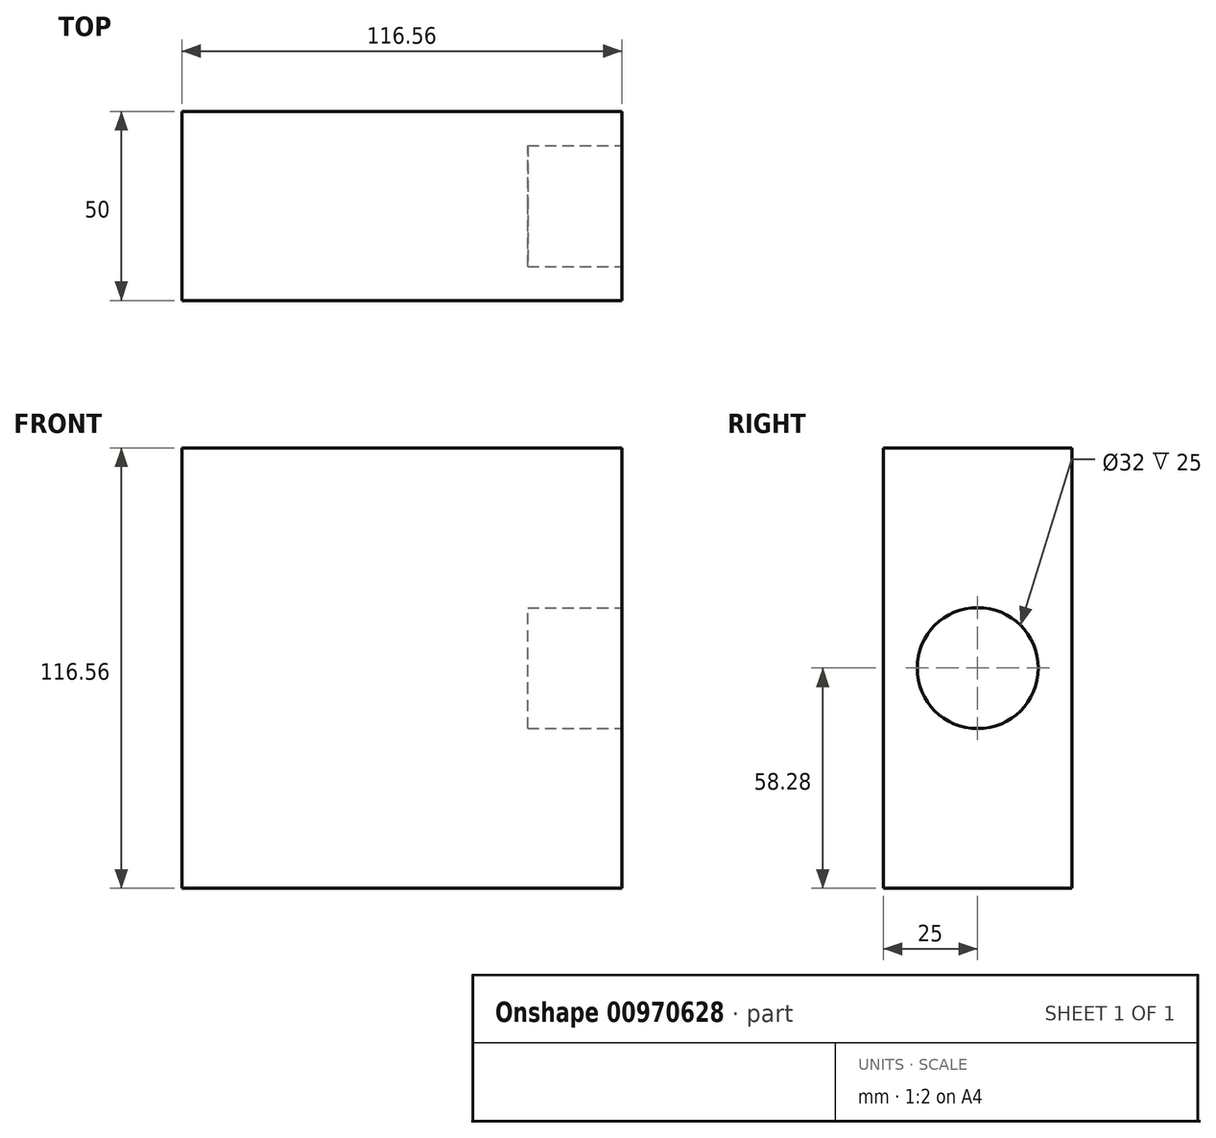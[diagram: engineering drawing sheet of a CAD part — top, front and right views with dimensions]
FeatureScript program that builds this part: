
annotation { "Feature Type Name" : "Feature", "Feature Type Description" : "" }
export const myFeature = defineFeature(function(context is Context, id is Id, definition is map)
    precondition{}
    {
        {
            var Q0;
            Q0=qCreatedBy(makeId("Front.planeOp"),FACE);
            var sketch = newSketch(context, id + "F0", { "sketchPlane" : qUnion([Q0])});
            skLineSegment(sketch, "E0.bottom", {"start": v(58.28, -58.28) * mm, "end": v(-58.28, -58.28) * mm});
            skLineSegment(sketch, "E0.top", {"start": v(58.28, 58.28) * mm, "end": v(-58.28, 58.28) * mm});
            skLineSegment(sketch, "E0.left", {"start": v(58.28, -58.28) * mm, "end": v(58.28, 58.28) * mm});
            skLineSegment(sketch, "E0.right", {"start": v(-58.28, -58.28) * mm, "end": v(-58.28, 58.28) * mm});
            skPoint(sketch, "E0.middle", {"position": v(0, 0) * mm});
            skSolve(sketch);
        }
        {
            var Q0;
            Q0=makeQuery(id+"F0.imprint","IMPRINT",FACE,{"disambiguationData":[TD([[makeQuery(id+"F0.imprint","IMPRINT",EDGE,{"derivedFrom":sQuery(id+"F0.wireOp",EDGE,"E0.bottom")}),-1.0]])]});
            extrude(context, id + "F1", {"entities" : qUnion([Q0]), "depth" : 50 * mm, "offsetDistance" : 25 * mm});
        }
        {
            var Q0;
            Q0=makeQuery(id+"F1.opExtrude","SWEPT_FACE",FACE,{"disambiguationData":[OSD([sQuery(id+"F0.wireOp",EDGE,"E0.left")])]});
            var sketch = newSketch(context, id + "F2", { "sketchPlane" : qUnion([Q0])});
            skCircle(sketch, "E1", {"center": v(-25, 0) * mm, "radius": 16 * mm});
            skLineSegment(sketch, "E2", {"start": v(-25, -58.28) * mm, "end": v(-25, 58.28) * mm, "construction": true});
            skSolve(sketch);
        }
        {
            var Q0;
            Q0=makeQuery(id+"F2.imprint","IMPRINT",FACE,{"disambiguationData":[TD([[makeQuery(id+"F2.imprint","IMPRINT",EDGE,{"derivedFrom":sQuery(id+"F2.wireOp",EDGE,"E1")}),1.0]])]});
            var Q1;
            Q1=sQuery(id+"F2.wireOp",EDGE,"E1");
            extrude(context, id + "F3", {"entities" : qUnion([Q0]), "operationType" : NewBodyOperationType.REMOVE, "surfaceEntities" : qUnion([Q1]), "oppositeDirection" : true, "depth" : 25 * mm, "offsetDistance" : 25 * mm});
        }
    });
